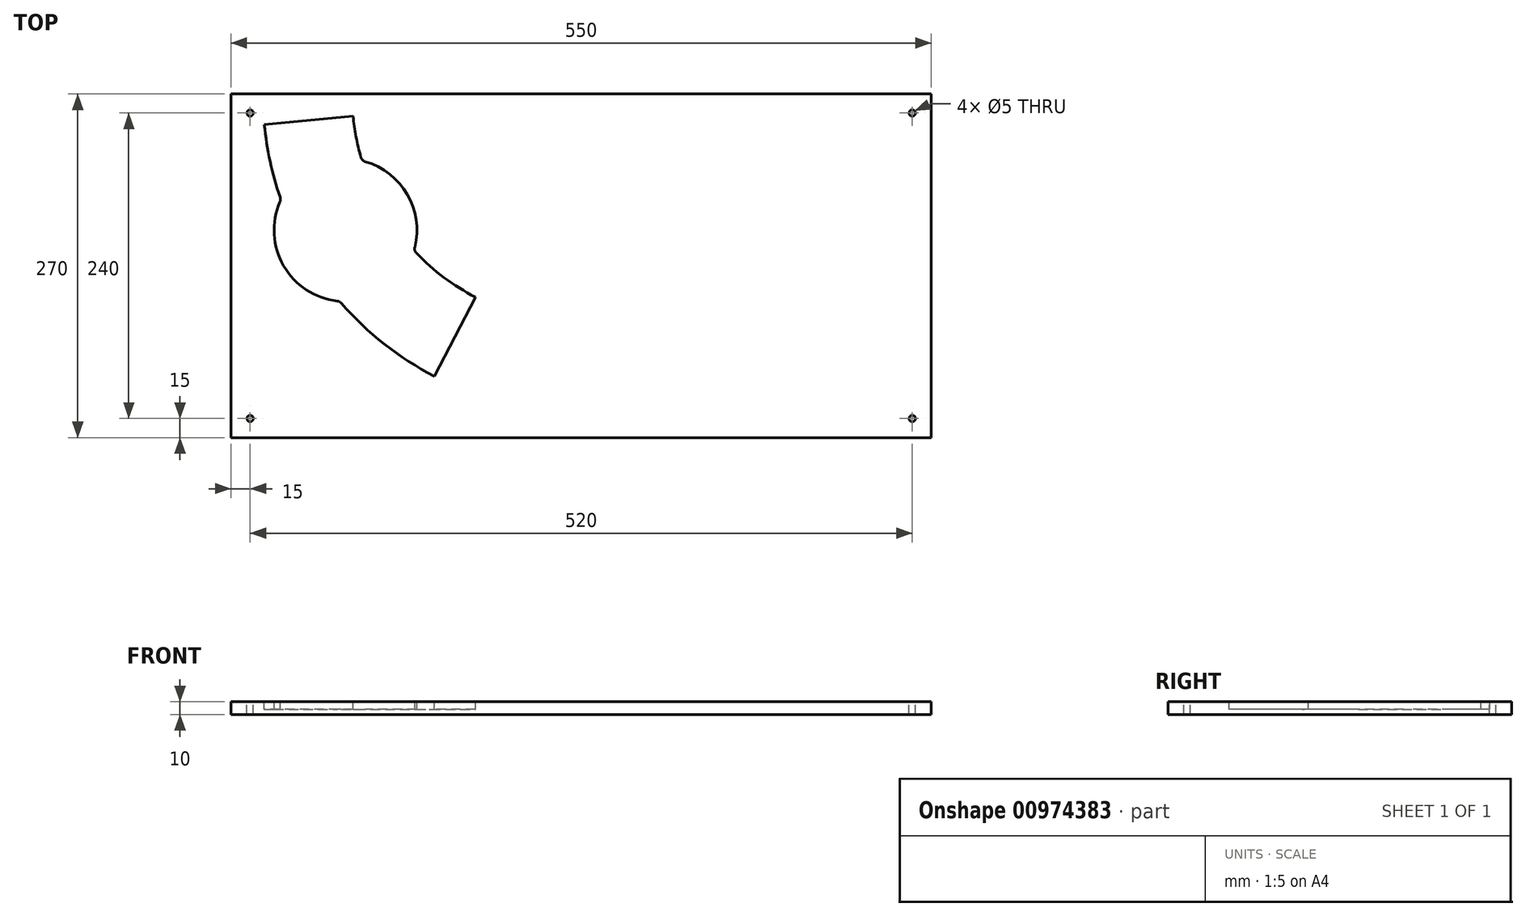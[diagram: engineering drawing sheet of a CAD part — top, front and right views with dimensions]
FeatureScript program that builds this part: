
annotation { "Feature Type Name" : "Feature", "Feature Type Description" : "" }
export const myFeature = defineFeature(function(context is Context, id is Id, definition is map)
    precondition{}
    {
        {
            var Q0;
            Q0=qCreatedBy(makeId("Top.planeOp"),FACE);
            var sketch = newSketch(context, id + "F0", { "sketchPlane" : qUnion([Q0])});
            skLineSegment(sketch, "E0.bottom", {"start": v(0, 0) * mm, "end": v(550, 0) * mm});
            skLineSegment(sketch, "E0.top", {"start": v(0, -270) * mm, "end": v(550, -270) * mm});
            skLineSegment(sketch, "E0.left", {"start": v(0, 0) * mm, "end": v(0, -270) * mm});
            skLineSegment(sketch, "E0.right", {"start": v(550, 0) * mm, "end": v(550, -270) * mm});
            skSolve(sketch);
        }
        {
            var Q0;
            Q0=makeQuery(id+"F0.imprint","IMPRINT",FACE,{"disambiguationData":[TD([[makeQuery(id+"F0.imprint","IMPRINT",EDGE,{"derivedFrom":sQuery(id+"F0.wireOp",EDGE,"E0.bottom")}),-1.0]])]});
            extrude(context, id + "F1", {"entities" : qUnion([Q0]), "oppositeDirection" : true, "depth" : 10 * mm, "offsetDistance" : 25 * mm});
        }
        {
            var Q0;
            Q0=makeQuery(id+"F1.opExtrude","CAP_FACE",FACE,{"disambiguationData":[OSD([sQuery(id+"F0.wireOp",EDGE,"E0.bottom"),sQuery(id+"F0.wireOp",EDGE,"E0.top"),sQuery(id+"F0.wireOp",EDGE,"E0.left"),sQuery(id+"F0.wireOp",EDGE,"E0.right")])],"isStart":true});
            var sketch = newSketch(context, id + "F2", { "sketchPlane" : qUnion([Q0])});
            skArc(sketch, "E1", {"start": v(26.15, -24) * mm, "mid": v(195.26, -236.94) * mm, "end": v(458.7, -169.57) * mm});
            skArc(sketch, "E2", {"start": v(95.83, -17.28) * mm, "mid": v(209.67, -167.73) * mm, "end": v(395.28, -133.91) * mm});
            skPoint(sketch, "E3.start.orphan", {"position": v(275, -180) * mm});
            skCircle(sketch, "E4", {"center": v(460.77, -91.66) * mm, "radius": 77.94 * mm});
            skLineSegment(sketch, "E5", {"start": v(95.83, -17.28) * mm, "end": v(26.15, -24) * mm});
            skLineSegment(sketch, "E6", {"start": v(191.91, -159.67) * mm, "end": v(159.6, -221.77) * mm});
            skLineSegment(sketch, "E7", {"start": v(550, 0) * mm, "end": v(535, 0) * mm});
            skLineSegment(sketch, "E8", {"start": v(535, 0) * mm, "end": v(535, -15) * mm});
            skLineSegment(sketch, "E9", {"start": v(0, -270) * mm, "end": v(15, -270) * mm});
            skLineSegment(sketch, "E10", {"start": v(15, -270) * mm, "end": v(15, -255) * mm});
            skCircle(sketch, "E11", {"center": v(15, -255) * mm, "radius": 2.5 * mm});
            skCircle(sketch, "E12", {"center": v(535, -255) * mm, "radius": 2.5 * mm});
            skCircle(sketch, "E13", {"center": v(535, -15) * mm, "radius": 2.5 * mm});
            skCircle(sketch, "E14", {"center": v(15, -15) * mm, "radius": 2.5 * mm});
            skCircle(sketch, "E15", {"center": v(89.9, -107.02) * mm, "radius": 56.06 * mm});
            skCircle(sketch, "E16", {"center": v(275, 0) * mm, "radius": 182 * mm});
            skCircle(sketch, "E17", {"center": v(275, 0) * mm, "radius": 239.5 * mm});
            skSolve(sketch);
        }
        {
            var Q0;
            {var subQ0=sQuery(id+"F2.wireOp",EDGE,"E5");var subQ1=sQuery(id+"F2.wireOp",EDGE,"E2");var subQ2=makeQuery(id+"F2.imprint","INTERSECT",VERTEX,{"derivedFrom":[subQ1,subQ0]});Q0=makeQuery(id+"F2.imprint","IMPRINT",FACE,{"disambiguationData":[TD([[makeQuery(id+"F2.imprint","IMPRINT",EDGE,{"disambiguationData":[TD([[subQ2,-1.0]])],"derivedFrom":subQ1}),-1.0]])]});}
            var Q1;
            {var subQ0=sQuery(id+"F2.wireOp",EDGE,"E16");var subQ1=sQuery(id+"F2.wireOp",EDGE,"E5");var subQ2=makeQuery(id+"F2.imprint","INTERSECT",VERTEX,{"derivedFrom":[subQ1,subQ0]});Q1=makeQuery(id+"F2.imprint","IMPRINT",FACE,{"disambiguationData":[TD([[makeQuery(id+"F2.imprint","IMPRINT",EDGE,{"disambiguationData":[TD([[subQ2,-1.0]])],"derivedFrom":subQ1}),1.0]])]});}
            var Q2;
            {var subQ0=sQuery(id+"F2.wireOp",EDGE,"E5");var subQ1=sQuery(id+"F2.wireOp",EDGE,"E1");var subQ2=makeQuery(id+"F2.imprint","INTERSECT",VERTEX,{"derivedFrom":[subQ1,subQ0]});Q2=makeQuery(id+"F2.imprint","IMPRINT",FACE,{"disambiguationData":[TD([[makeQuery(id+"F2.imprint","IMPRINT",EDGE,{"disambiguationData":[TD([[subQ2,-1.0]])],"derivedFrom":subQ1}),1.0]])]});}
            var Q3;
            {var subQ0=sQuery(id+"F2.wireOp",EDGE,"E15");var subQ1=sQuery(id+"F2.wireOp",EDGE,"E1");var subQ2=makeQuery(id+"F2.imprint","INTERSECT",VERTEX,{"disambiguationData":[OD(0.0)],"derivedFrom":[subQ1,subQ0]});Q3=makeQuery(id+"F2.imprint","IMPRINT",FACE,{"disambiguationData":[TD([[makeQuery(id+"F2.imprint","IMPRINT",EDGE,{"disambiguationData":[TD([[subQ2,-1.0]])],"derivedFrom":subQ1}),-1.0]])]});}
            var Q4;
            {var subQ0=sQuery(id+"F2.wireOp",EDGE,"E15");var subQ1=sQuery(id+"F2.wireOp",EDGE,"E1");var subQ2=makeQuery(id+"F2.imprint","INTERSECT",VERTEX,{"disambiguationData":[OD(0.0)],"derivedFrom":[subQ1,subQ0]});Q4=makeQuery(id+"F2.imprint","IMPRINT",FACE,{"disambiguationData":[TD([[makeQuery(id+"F2.imprint","IMPRINT",EDGE,{"disambiguationData":[TD([[subQ2,-1.0]])],"derivedFrom":subQ1}),1.0]])]});}
            var Q5;
            {var subQ0=sQuery(id+"F2.wireOp",EDGE,"E16");var subQ1=sQuery(id+"F2.wireOp",EDGE,"E15");var subQ2=makeQuery(id+"F2.imprint","INTERSECT",VERTEX,{"disambiguationData":[OD(0.0)],"derivedFrom":[subQ1,subQ0]});Q5=makeQuery(id+"F2.imprint","IMPRINT",FACE,{"disambiguationData":[TD([[makeQuery(id+"F2.imprint","IMPRINT",EDGE,{"disambiguationData":[TD([[subQ2,-1.0]])],"derivedFrom":subQ1}),1.0]])]});}
            var Q6;
            {var subQ0=sQuery(id+"F2.wireOp",EDGE,"E15");var subQ1=sQuery(id+"F2.wireOp",EDGE,"E2");var subQ2=makeQuery(id+"F2.imprint","INTERSECT",VERTEX,{"disambiguationData":[OD(0.0)],"derivedFrom":[subQ1,subQ0]});Q6=makeQuery(id+"F2.imprint","IMPRINT",FACE,{"disambiguationData":[TD([[makeQuery(id+"F2.imprint","IMPRINT",EDGE,{"disambiguationData":[TD([[subQ2,-1.0]])],"derivedFrom":subQ1}),-1.0]])]});}
            var Q7;
            {var subQ0=sQuery(id+"F2.wireOp",EDGE,"E15");var subQ1=sQuery(id+"F2.wireOp",EDGE,"E2");var subQ2=makeQuery(id+"F2.imprint","INTERSECT",VERTEX,{"disambiguationData":[OD(0.0)],"derivedFrom":[subQ1,subQ0]});Q7=makeQuery(id+"F2.imprint","IMPRINT",FACE,{"disambiguationData":[TD([[makeQuery(id+"F2.imprint","IMPRINT",EDGE,{"disambiguationData":[TD([[subQ2,-1.0]])],"derivedFrom":subQ1}),1.0]])]});}
            var Q8;
            {var subQ0=sQuery(id+"F2.wireOp",EDGE,"E6");var subQ1=sQuery(id+"F2.wireOp",EDGE,"E2");var subQ2=makeQuery(id+"F2.imprint","INTERSECT",VERTEX,{"derivedFrom":[subQ1,subQ0]});Q8=makeQuery(id+"F2.imprint","IMPRINT",FACE,{"disambiguationData":[TD([[makeQuery(id+"F2.imprint","IMPRINT",EDGE,{"disambiguationData":[TD([[subQ2,1.0]])],"derivedFrom":subQ1}),-1.0]])]});}
            var Q9;
            {var subQ0=sQuery(id+"F2.wireOp",EDGE,"E16");var subQ1=sQuery(id+"F2.wireOp",EDGE,"E6");var subQ2=makeQuery(id+"F2.imprint","INTERSECT",VERTEX,{"derivedFrom":[subQ1,subQ0]});Q9=makeQuery(id+"F2.imprint","IMPRINT",FACE,{"disambiguationData":[TD([[makeQuery(id+"F2.imprint","IMPRINT",EDGE,{"disambiguationData":[TD([[subQ2,-1.0]])],"derivedFrom":subQ1}),-1.0]])]});}
            var Q10;
            {var subQ0=sQuery(id+"F2.wireOp",EDGE,"E6");var subQ1=sQuery(id+"F2.wireOp",EDGE,"E1");var subQ2=makeQuery(id+"F2.imprint","INTERSECT",VERTEX,{"derivedFrom":[subQ1,subQ0]});Q10=makeQuery(id+"F2.imprint","IMPRINT",FACE,{"disambiguationData":[TD([[makeQuery(id+"F2.imprint","IMPRINT",EDGE,{"disambiguationData":[TD([[subQ2,1.0]])],"derivedFrom":subQ1}),1.0]])]});}
            extrude(context, id + "F3", {"entities" : qUnion([Q0, Q1, Q2, Q3, Q4, Q5, Q6, Q7, Q8, Q9, Q10]), "operationType" : NewBodyOperationType.REMOVE, "oppositeDirection" : true, "depth" : 6 * mm, "offsetDistance" : 25 * mm});
        }
        {
            var Q0;
            Q0=makeQuery(id+"F2.imprint","IMPRINT",FACE,{"disambiguationData":[TD([[makeQuery(id+"F2.imprint","IMPRINT",EDGE,{"derivedFrom":sQuery(id+"F2.wireOp",EDGE,"E11")}),1.0]])]});
            var Q1;
            Q1=makeQuery(id+"F2.imprint","IMPRINT",FACE,{"disambiguationData":[TD([[makeQuery(id+"F2.imprint","IMPRINT",EDGE,{"derivedFrom":sQuery(id+"F2.wireOp",EDGE,"E14")}),1.0]])]});
            var Q2;
            Q2=makeQuery(id+"F2.imprint","IMPRINT",FACE,{"disambiguationData":[TD([[makeQuery(id+"F2.imprint","IMPRINT",EDGE,{"derivedFrom":sQuery(id+"F2.wireOp",EDGE,"E13")}),1.0]])]});
            var Q3;
            Q3=makeQuery(id+"F2.imprint","IMPRINT",FACE,{"disambiguationData":[TD([[makeQuery(id+"F2.imprint","IMPRINT",EDGE,{"derivedFrom":sQuery(id+"F2.wireOp",EDGE,"E12")}),1.0]])]});
            extrude(context, id + "F4", {"entities" : qUnion([Q0, Q1, Q2, Q3]), "operationType" : NewBodyOperationType.REMOVE, "oppositeDirection" : true, "depth" : 25 * mm, "offsetDistance" : 25 * mm});
        }
        {
            var Q0;
            {var subQ0=sQuery(id+"F2.wireOp",EDGE,"E15");var subQ1=sQuery(id+"F2.wireOp",EDGE,"E2");Q0=makeQuery(id+"F3.boolean.opBoolean","COPY",EDGE,{"derivedFrom":makeQuery(id+"F3.opExtrude","SWEPT_EDGE",EDGE,{"disambiguationData":[OSD([subQ1,subQ0]),TDD([makeQuery(id+"F2.imprint","INTERSECT",VERTEX,{"disambiguationData":[OD(0.0)],"derivedFrom":[subQ1,subQ0]})])]})});}
            var Q1;
            {var subQ0=sQuery(id+"F2.wireOp",EDGE,"E15");var subQ1=sQuery(id+"F2.wireOp",EDGE,"E2");Q1=makeQuery(id+"F3.boolean.opBoolean","COPY",EDGE,{"derivedFrom":makeQuery(id+"F3.opExtrude","SWEPT_EDGE",EDGE,{"disambiguationData":[OSD([subQ1,subQ0]),TDD([makeQuery(id+"F2.imprint","INTERSECT",VERTEX,{"disambiguationData":[OD(1.0)],"derivedFrom":[subQ1,subQ0]})])]})});}
            var Q2;
            {var subQ0=sQuery(id+"F2.wireOp",EDGE,"E15");var subQ1=sQuery(id+"F2.wireOp",EDGE,"E1");Q2=makeQuery(id+"F3.boolean.opBoolean","COPY",EDGE,{"derivedFrom":makeQuery(id+"F3.opExtrude","SWEPT_EDGE",EDGE,{"disambiguationData":[OSD([subQ1,subQ0]),TDD([makeQuery(id+"F2.imprint","INTERSECT",VERTEX,{"disambiguationData":[OD(1.0)],"derivedFrom":[subQ1,subQ0]})])]})});}
            var Q3;
            {var subQ0=sQuery(id+"F2.wireOp",EDGE,"E15");var subQ1=sQuery(id+"F2.wireOp",EDGE,"E1");Q3=makeQuery(id+"F3.boolean.opBoolean","COPY",EDGE,{"derivedFrom":makeQuery(id+"F3.opExtrude","SWEPT_EDGE",EDGE,{"disambiguationData":[OSD([subQ1,subQ0]),TDD([makeQuery(id+"F2.imprint","INTERSECT",VERTEX,{"disambiguationData":[OD(0.0)],"derivedFrom":[subQ1,subQ0]})])]})});}
            fillet(context, id + "F5", {"entities" : qUnion([Q0, Q1, Q2, Q3]), "radius" : 5 * mm, "tangentPropagation" : true, "allowEdgeOverflow" : false});
        }
    });
